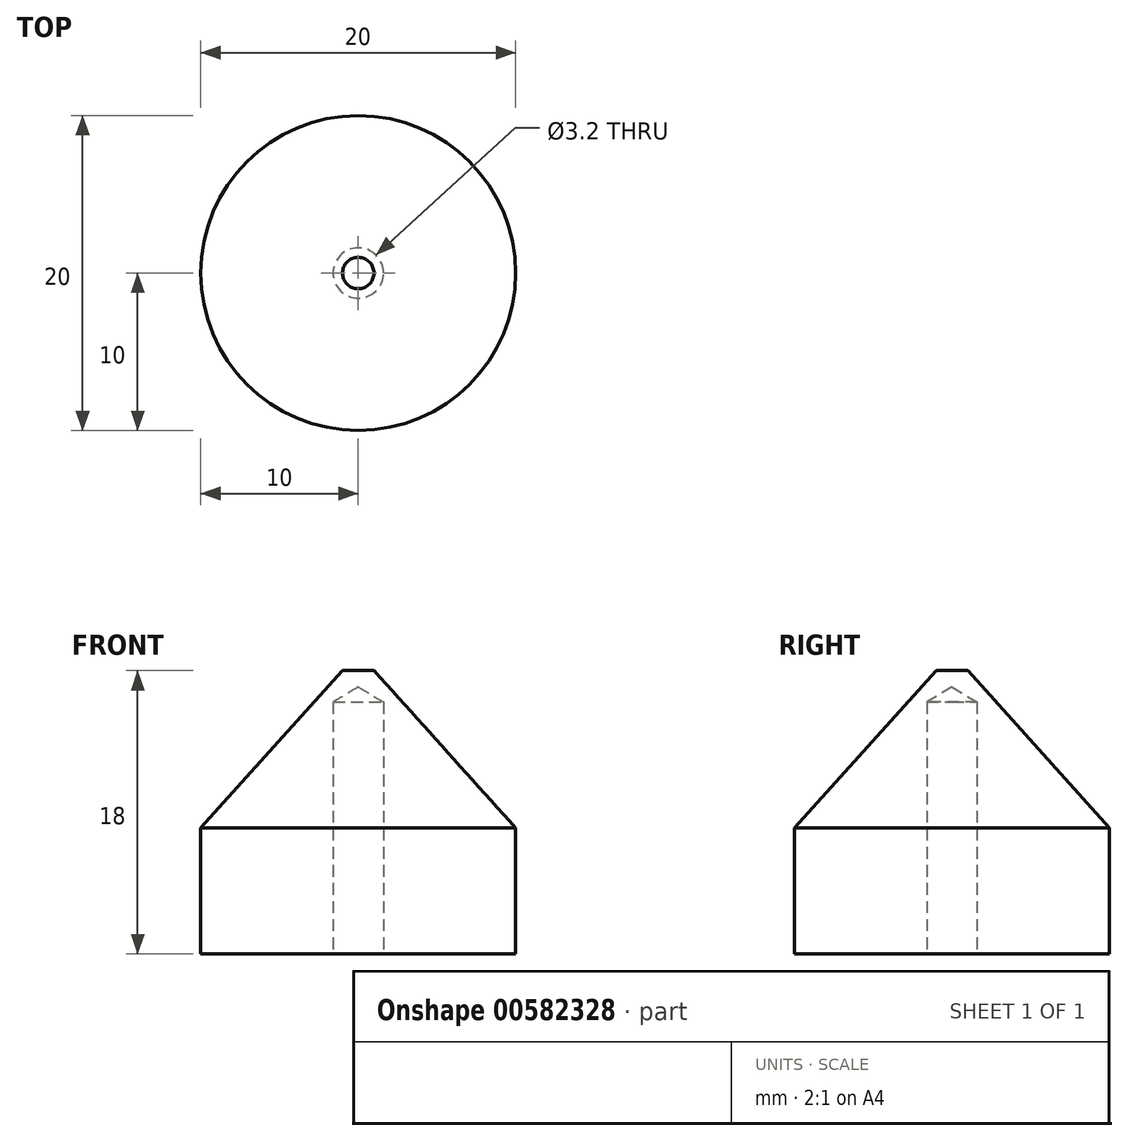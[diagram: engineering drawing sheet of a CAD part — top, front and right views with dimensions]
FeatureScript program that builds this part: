
annotation { "Feature Type Name" : "Feature", "Feature Type Description" : "" }
export const myFeature = defineFeature(function(context is Context, id is Id, definition is map)
    precondition{}
    {
        {
            var Q0;
            Q0=qCreatedBy(makeId("Top.planeOp"),FACE);
            var sketch = newSketch(context, id + "F0", { "sketchPlane" : qUnion([Q0])});
            skCircle(sketch, "E0", {"center": v(0, 0) * mm, "radius": 10 * mm});
            skCircle(sketch, "E1", {"center": v(0, 0) * mm, "radius": 6.1 * mm});
            skSolve(sketch);
        }
        {
            var Q0;
            Q0=qSketchRegion(id+"F0",true);
            var Q1;
            Q1=makeQuery(id+"F0.imprint","IMPRINT",FACE,{"disambiguationData":[TD([[makeQuery(id+"F0.imprint","IMPRINT",EDGE,{"derivedFrom":sQuery(id+"F0.wireOp",EDGE,"E1")}),1.0]])]});
            extrude(context, id + "F1", {"entities" : qUnion([Q0, Q1]), "depth" : 6 * mm, "offsetDistance" : 25 * mm});
        }
        {
            var Q0;
            Q0=makeQuery(id+"F0.imprint","IMPRINT",FACE,{"disambiguationData":[TD([[makeQuery(id+"F0.imprint","IMPRINT",EDGE,{"derivedFrom":sQuery(id+"F0.wireOp",EDGE,"E0")}),1.0]])]});
            extrude(context, id + "F2", {"entities" : qUnion([Q0]), "operationType" : NewBodyOperationType.ADD, "oppositeDirection" : true, "depth" : 10 * mm, "offsetDistance" : 25 * mm});
        }
        {
            var Q0;
            Q0=makeQuery(id+"F1.opExtrude","CAP_FACE",FACE,{"disambiguationData":[OSD([sQuery(id+"F0.wireOp",EDGE,"E0")])],"isStart":false});
            cPlane(context, id + "F3", {"entities" : qUnion([Q0]), "cplaneType" : CPlaneType.OFFSET, "offset" : 10 * mm, "width" : 150 * mm, "height" : 150 * mm});
        }
        {
            var Q0;
            Q0=qCreatedBy(id+"F3.planeOp",FACE);
            var sketch = newSketch(context, id + "F4", { "sketchPlane" : qUnion([Q0])});
            skCircle(sketch, "E2", {"center": v(0, 0) * mm, "radius": 1 * mm});
            skSolve(sketch);
        }
        {
            var Q0;
            Q0=makeQuery(id+"F4.imprint","IMPRINT",FACE,{"disambiguationData":[TD([[makeQuery(id+"F4.imprint","IMPRINT",EDGE,{"derivedFrom":sQuery(id+"F4.wireOp",EDGE,"E2")}),1.0]])]});
            var Q1;
            Q1=makeQuery(id+"F1.opExtrude","CAP_FACE",FACE,{"disambiguationData":[OSD([sQuery(id+"F0.wireOp",EDGE,"E0")])],"isStart":false});
            var Q2;
            {var subQ0=sQuery(id+"F0.wireOp",EDGE,"E0");Q2=makeQuery(id+"F6.imprint","IMPRINT",FACE,{"disambiguationData":[TD([[makeQuery(id+"F6.imprint","IMPRINT",EDGE,{"derivedFrom":makeQuery(id+"F1.opExtrude","CAP_EDGE",EDGE,{"disambiguationData":[OSD([subQ0])],"isStart":false})}),1.0]])]});}
            var Q3;
            Q3=sQuery(id+"F4.wireOp",EDGE,"E2");
            loft(context, id + "F5", {"sheetProfilesArray" : [{ "sheetProfileEntities" : qUnion([Q0]) }, { "sheetProfileEntities" : qUnion([Q1]) }], "wireProfilesArray" : [{ "wireProfileEntities" : qUnion([Q2]) }, { "wireProfileEntities" : qUnion([Q3]) }]});
        }
        {
            var Q0;
            Q0=makeQuery(id+"F1.opExtrude","CAP_FACE",FACE,{"disambiguationData":[OSD([sQuery(id+"F0.wireOp",EDGE,"E0")])],"isStart":false});
            var sketch = newSketch(context, id + "F6", { "sketchPlane" : qUnion([Q0])});
            skSolve(sketch);
        }
        {
            var Q0;
            Q0=sQuery(id+"F0.wireOp",VERTEX,"E0.center");
            var Q1;
            Q1=makeQuery(id+"F1.opExtrude","SWEPT_BODY",BODY,{"disambiguationData":[OSD([sQuery(id+"F0.wireOp",EDGE,"E0")])]});
            hole(context, id + "F7", {"style" : HoleStyle.C_BORE, "endStyle" : HoleEndStyle.THROUGH, "oppositeDirection" : true, "holeDiameter" : 4.2 * mm, "cBoreDiameter" : 7 * mm, "cBoreDepth" : 4 * mm, "majorDiameter" : 5 * mm, "isTappedThrough" : true, "tappedDepth" : 12 * mm, "tapClearance" : 3, "locations" : qUnion([Q0]), "scope" : qUnion([Q1])});
        }
        {
            var Q0;
            Q0=sQuery(id+"F0.wireOp",VERTEX,"E0.center");
            var Q1;
            Q1=makeQuery(id+"F5.opLoft","SWEPT_BODY",BODY,{"disambiguationData":[OSD([sQuery(id+"F0.wireOp",EDGE,"E0"),makeQuery(id+"F4.imprint","IMPRINT",FACE,{"disambiguationData":[TD([[makeQuery(id+"F4.imprint","IMPRINT",EDGE,{"derivedFrom":sQuery(id+"F4.wireOp",EDGE,"E2")}),1.0]])]})])]});
            hole(context, id + "F8", {"style" : HoleStyle.SIMPLE, "endStyle" : HoleEndStyle.BLIND, "oppositeDirection" : true, "holeDiameter" : 3.2 * mm, "majorDiameter" : 5 * mm, "holeDepth" : 8 * mm, "isTappedThrough" : true, "tappedDepth" : 12 * mm, "tapClearance" : 3, "locations" : qUnion([Q0]), "scope" : qUnion([Q1])});
        }
        {
            var Q0;
            Q0=makeQuery(id+"F1.opExtrude","SWEPT_BODY",BODY,{"disambiguationData":[OSD([sQuery(id+"F0.wireOp",EDGE,"E0")])]});
            deleteBodies(context, id + "F9", {"entities" : qUnion([Q0])});
        }
        {
            var Q0;
            Q0=makeQuery(id+"F6.imprint","IMPRINT",FACE,{"disambiguationData":[TD([[makeQuery(id+"F6.imprint","IMPRINT",EDGE,{"derivedFrom":makeQuery(id+"F1.opExtrude","CAP_EDGE",EDGE,{"disambiguationData":[OSD([sQuery(id+"F0.wireOp",EDGE,"E0")])],"isStart":false})}),1.0]])]});
            extrude(context, id + "F10", {"entities" : qUnion([Q0]), "operationType" : NewBodyOperationType.ADD, "oppositeDirection" : true, "depth" : 8 * mm, "offsetDistance" : 25 * mm});
        }
        {
            var Q0;
            Q0=makeQuery(id+"F10.opExtrude","CAP_FACE",FACE,{"disambiguationData":[OSD([sQuery(id+"F0.wireOp",EDGE,"E0")])],"isStart":false});
            var sketch = newSketch(context, id + "F11", { "sketchPlane" : qUnion([Q0])});
            skLineSegment(sketch, "E3", {"start": v(0, 0) * mm, "end": v(-10, 0) * mm});
            skCircle(sketch, "E4", {"center": v(0, 0) * mm, "radius": 1.6 * mm});
            skSolve(sketch);
        }
        {
            var Q0;
            Q0=makeQuery(id+"F11.imprint","IMPRINT",FACE,{"disambiguationData":[TD([[makeQuery(id+"F11.imprint","IMPRINT",EDGE,{"derivedFrom":sQuery(id+"F11.wireOp",EDGE,"E4")}),1.0]])]});
            extrude(context, id + "F12", {"entities" : qUnion([Q0]), "operationType" : NewBodyOperationType.REMOVE, "oppositeDirection" : true, "depth" : 10 * mm, "offsetDistance" : 25 * mm});
        }
    });
